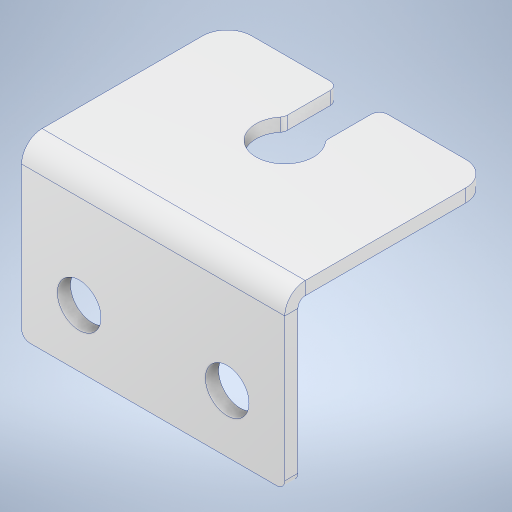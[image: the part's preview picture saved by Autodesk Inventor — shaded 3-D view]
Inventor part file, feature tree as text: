
AUTODESK INVENTOR PART (.ipt)
format: ipt  version: 2024 (Build 280153000, 153)  size: 303,616 bytes
history: native  units: mm
features: sheet_metal_op x4, fillet x4, other x2, sketch x2, hole x1, extrude x1, projected_geometry x1
ambient origin geometry x8: Origin, YZ Plane, XZ Plane, XY Plane, X Axis, Y Axis, Z Axis, Center Point
bodies: Body1 (feature_tree)
feature tree (15):
  sheet_metal_op  "Face2"
  fillet  "Fillet7"  Radius=36.0mm
  hole  "Hole4"  [1 undecoded]
  sheet_metal_op  "Flange5"
  fillet  "Fillet8"  Radius=14.0mm
  extrude  "Extrusion7"  Depth=1.0mm
  fillet  "Fillet9"  Radius=1.0mm
  fillet  "Fillet10"  Radius=20.594885mm
  other  "Plate4"
  sketch  "Sketch10"  dims[d71=1.6002mm d126=32.0mm d127=14.0mm]
  other  "Plate7"
  sheet_metal_op  "Bend5"
  sheet_metal_op  "Corner5"
  sketch  "Sketch11"  dims[d128=7.0mm d129=12.25mm d130=1.0mm d131=5.3mm d132=6.0mm d133=4.0mm d134=2.0mm d135=90.0deg d136=1.6002mm d137=20.594885mm d138=1.6002mm d139=0.8001mm d140=3.2004mm d141=0.889mm d142=25.0mm d143=90.0deg d144=0.889mm d145=6.4008mm d146=1.6002mm d147=0.889mm d148=3.0mm d149=7.0mm d150=9.0mm d151=5.0mm d152=0.0mm d153=0.0mm d154=1.0mm d155=1.0mm d123=0.5mm d124=0.872665mm d125=0.5mm]
  projected_geometry  "Projected Loop3"
note: 1 required parameter value undecoded (feature->parameter linkage not recoverable at this tier; creation-order binding heuristic only, values carry confidence <= 0.55)
